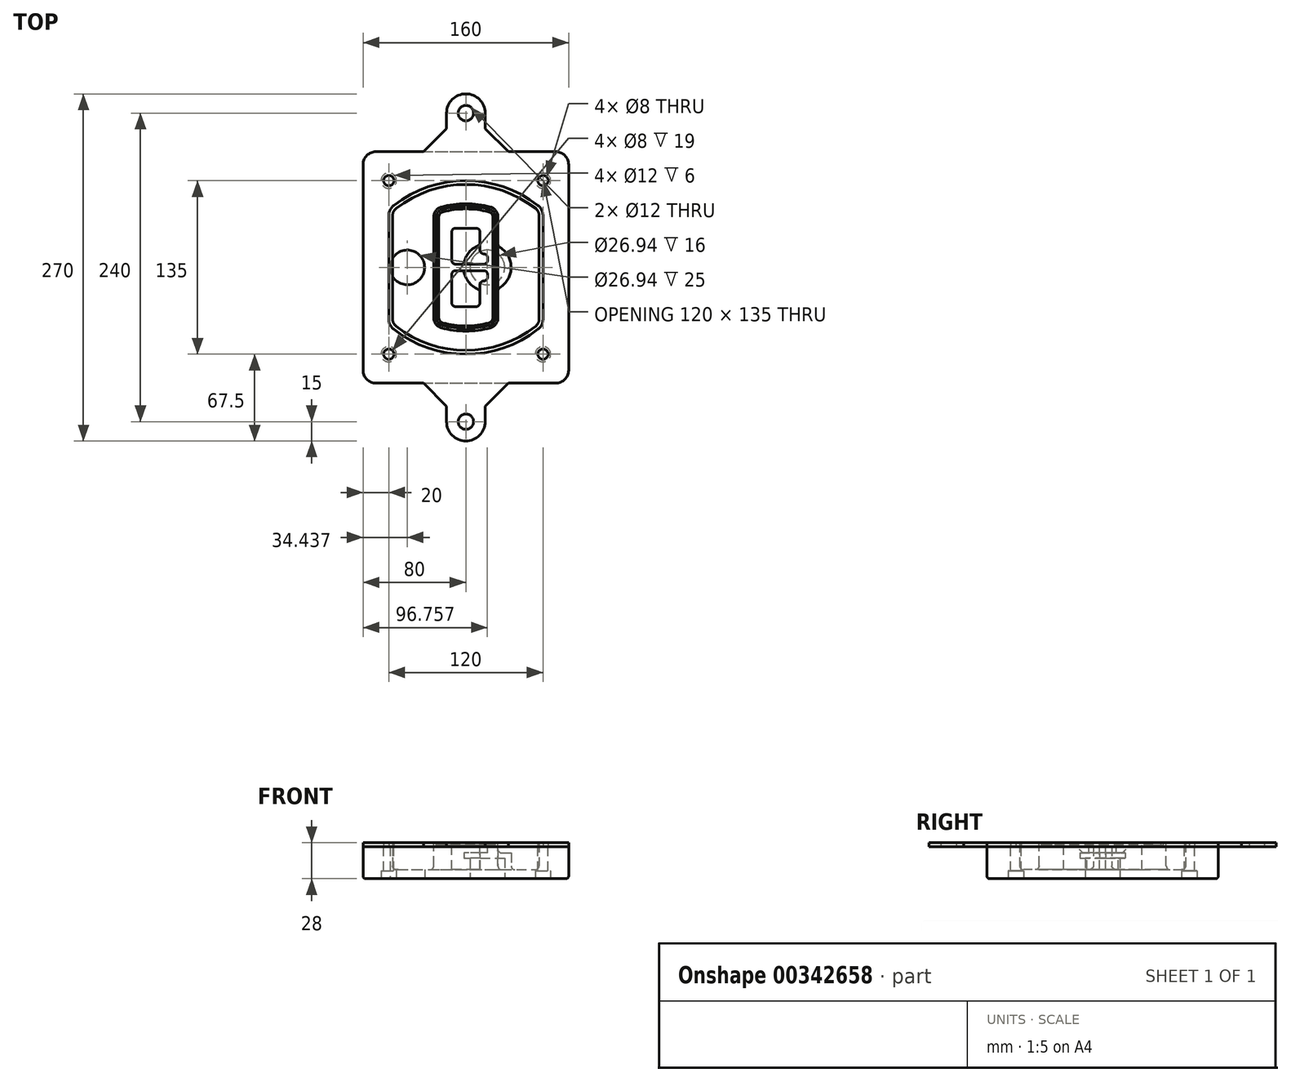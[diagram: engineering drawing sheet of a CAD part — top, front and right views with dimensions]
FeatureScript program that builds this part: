
annotation { "Feature Type Name" : "Feature", "Feature Type Description" : "" }
export const myFeature = defineFeature(function(context is Context, id is Id, definition is map)
    precondition{}
    {
        {
            var Q0;
            Q0=qCreatedBy(makeId("Top.planeOp"),FACE);
            var sketch = newSketch(context, id + "F0", { "sketchPlane" : qUnion([Q0])});
            skPoint(sketch, "E0.rect.middle", {"position": v(0, 0) * mm});
            skLineSegment(sketch, "E1.bottom", {"start": v(-70, -90) * mm, "end": v(70, -90) * mm});
            skLineSegment(sketch, "E1.top", {"start": v(-70, 90) * mm, "end": v(70, 90) * mm});
            skLineSegment(sketch, "E1.left", {"start": v(-80, -80) * mm, "end": v(-80, 80) * mm});
            skLineSegment(sketch, "E1.right", {"start": v(80, -80) * mm, "end": v(80, 80) * mm});
            skLineSegment(sketch, "E2", {"start": v(-80, 90) * mm, "end": v(80, -90) * mm, "construction": true});
            skLineSegment(sketch, "E3", {"start": v(80, 90) * mm, "end": v(-80, -90) * mm, "construction": true});
            skCircle(sketch, "E4", {"center": v(-60, 67.5) * mm, "radius": 4 * mm});
            skCircle(sketch, "E5", {"center": v(60, 67.5) * mm, "radius": 4 * mm});
            skCircle(sketch, "E6", {"center": v(60, -67.5) * mm, "radius": 4 * mm});
            skCircle(sketch, "E7", {"center": v(-60, -67.5) * mm, "radius": 4 * mm});
            skLineSegment(sketch, "E8", {"start": v(-60, 67.5) * mm, "end": v(60, 67.5) * mm, "construction": true});
            skLineSegment(sketch, "E9", {"start": v(60, 67.5) * mm, "end": v(60, -67.5) * mm, "construction": true});
            skLineSegment(sketch, "E10", {"start": v(60, -67.5) * mm, "end": v(-60, -67.5) * mm, "construction": true});
            skLineSegment(sketch, "E11", {"start": v(-60, -67.5) * mm, "end": v(-60, 67.5) * mm, "construction": true});
            skLineSegment(sketch, "E12", {"start": v(-60, 40.3) * mm, "end": v(-60, -40.3) * mm});
            skLineSegment(sketch, "E13", {"start": v(60, 40.3) * mm, "end": v(60, -40.3) * mm});
            skArc(sketch, "E14", {"start": v(56.15, 48.18) * mm, "mid": v(0, 67.5) * mm, "end": v(-56.15, 48.18) * mm});
            skArc(sketch, "E15", {"start": v(-56.15, -48.18) * mm, "mid": v(0, -67.5) * mm, "end": v(56.15, -48.18) * mm});
            skLineSegment(sketch, "E16", {"start": v(-60, 0) * mm, "end": v(60, 0) * mm, "construction": true});
            skPoint(sketch, "E17.visualSharp", {"position": v(-60, -45) * mm});
            skArc(sketch, "E17.filletArc", {"start": v(-60, -40.3) * mm, "mid": v(-58.99, -44.68) * mm, "end": v(-56.15, -48.18) * mm});
            skPoint(sketch, "E18.visualSharp", {"position": v(-60, 45) * mm});
            skArc(sketch, "E18.filletArc", {"start": v(-56.15, 48.18) * mm, "mid": v(-58.99, 44.68) * mm, "end": v(-60, 40.3) * mm});
            skPoint(sketch, "E19.visualSharp", {"position": v(60, 45) * mm});
            skArc(sketch, "E19.filletArc", {"start": v(60, 40.3) * mm, "mid": v(58.99, 44.68) * mm, "end": v(56.15, 48.18) * mm});
            skPoint(sketch, "E20.visualSharp", {"position": v(60, -45) * mm});
            skArc(sketch, "E20.filletArc", {"start": v(56.15, -48.18) * mm, "mid": v(58.99, -44.68) * mm, "end": v(60, -40.3) * mm});
            skPoint(sketch, "E21.visualSharp", {"position": v(-80, 90) * mm});
            skArc(sketch, "E21.filletArc", {"start": v(-70, 90) * mm, "mid": v(-77.07, 87.07) * mm, "end": v(-80, 80) * mm});
            skPoint(sketch, "E22.visualSharp", {"position": v(80, 90) * mm});
            skArc(sketch, "E22.filletArc", {"start": v(80, 80) * mm, "mid": v(77.07, 87.07) * mm, "end": v(70, 90) * mm});
            skPoint(sketch, "E23.visualSharp", {"position": v(80, -90) * mm});
            skArc(sketch, "E23.filletArc", {"start": v(70, -90) * mm, "mid": v(77.07, -87.07) * mm, "end": v(80, -80) * mm});
            skPoint(sketch, "E24.visualSharp", {"position": v(-80, -90) * mm});
            skArc(sketch, "E24.filletArc", {"start": v(-80, -80) * mm, "mid": v(-77.07, -87.07) * mm, "end": v(-70, -90) * mm});
            skArc(sketch, "E25.0", {"start": v(57, 40.3) * mm, "mid": v(56.3, 43.36) * mm, "end": v(54.3, 45.81) * mm});
            skLineSegment(sketch, "E25.1", {"start": v(57, 40.3) * mm, "end": v(57, -40.3) * mm});
            skArc(sketch, "E25.2", {"start": v(54.3, -45.81) * mm, "mid": v(56.3, -43.36) * mm, "end": v(57, -40.3) * mm});
            skArc(sketch, "E25.3", {"start": v(-54.3, -45.81) * mm, "mid": v(0, -64.5) * mm, "end": v(54.3, -45.81) * mm});
            skArc(sketch, "E25.4", {"start": v(-57, -40.3) * mm, "mid": v(-56.3, -43.36) * mm, "end": v(-54.3, -45.81) * mm});
            skArc(sketch, "E25.5", {"start": v(54.3, 45.81) * mm, "mid": v(0, 64.5) * mm, "end": v(-54.3, 45.81) * mm});
            skLineSegment(sketch, "E25.6", {"start": v(-57, 40.3) * mm, "end": v(-57, -40.3) * mm});
            skArc(sketch, "E25.7", {"start": v(-54.3, 45.81) * mm, "mid": v(-56.3, 43.36) * mm, "end": v(-57, 40.3) * mm});
            skArc(sketch, "E26.0", {"start": v(-58.62, 51.33) * mm, "mid": v(-62.58, 46.43) * mm, "end": v(-64, 40.3) * mm});
            skArc(sketch, "E26.1", {"start": v(58.62, 51.33) * mm, "mid": v(0, 71.5) * mm, "end": v(-58.62, 51.33) * mm});
            skArc(sketch, "E26.2", {"start": v(64, 40.3) * mm, "mid": v(62.58, 46.43) * mm, "end": v(58.62, 51.33) * mm});
            skLineSegment(sketch, "E26.3", {"start": v(64, 40.3) * mm, "end": v(64, -40.3) * mm});
            skArc(sketch, "E26.4", {"start": v(58.62, -51.33) * mm, "mid": v(62.58, -46.43) * mm, "end": v(64, -40.3) * mm});
            skLineSegment(sketch, "E26.5", {"start": v(-64, 40.3) * mm, "end": v(-64, -40.3) * mm});
            skArc(sketch, "E26.6", {"start": v(-58.62, -51.33) * mm, "mid": v(0, -71.5) * mm, "end": v(58.62, -51.33) * mm});
            skArc(sketch, "E26.7", {"start": v(-64, -40.3) * mm, "mid": v(-62.58, -46.43) * mm, "end": v(-58.62, -51.33) * mm});
            skSolve(sketch);
        }
        {
            var Q0;
            Q0=makeQuery(id+"F0.imprint","IMPRINT",FACE,{"disambiguationData":[TD([[makeQuery(id+"F0.imprint","IMPRINT",EDGE,{"derivedFrom":sQuery(id+"F0.wireOp",EDGE,"E1.bottom")}),1.0]])]});
            var Q1;
            Q1=makeQuery(id+"F0.imprint","IMPRINT",FACE,{"disambiguationData":[TD([[makeQuery(id+"F0.imprint","IMPRINT",EDGE,{"derivedFrom":sQuery(id+"F0.wireOp",EDGE,"E12")}),1.0]])]});
            var Q2;
            Q2=makeQuery(id+"F0.imprint","IMPRINT",FACE,{"disambiguationData":[TD([[makeQuery(id+"F0.imprint","IMPRINT",EDGE,{"derivedFrom":sQuery(id+"F0.wireOp",EDGE,"E25.0")}),1.0]])]});
            var Q3;
            Q3=makeQuery(id+"F0.imprint","IMPRINT",FACE,{"disambiguationData":[TD([[makeQuery(id+"F0.imprint","IMPRINT",EDGE,{"derivedFrom":sQuery(id+"F0.wireOp",EDGE,"E12")}),-1.0]])]});
            extrude(context, id + "F1", {"entities" : qUnion([Q0, Q1, Q2, Q3]), "oppositeDirection" : true, "depth" : 25 * mm});
        }
        {
            var Q0;
            Q0=makeQuery(id+"F0.imprint","IMPRINT",FACE,{"disambiguationData":[TD([[makeQuery(id+"F0.imprint","IMPRINT",EDGE,{"derivedFrom":sQuery(id+"F0.wireOp",EDGE,"E12")}),1.0]])]});
            extrude(context, id + "F2", {"entities" : qUnion([Q0]), "operationType" : NewBodyOperationType.ADD, "depth" : 3 * mm});
        }
        {
            var Q0;
            Q0=makeQuery(id+"F0.imprint","IMPRINT",FACE,{"disambiguationData":[TD([[makeQuery(id+"F0.imprint","IMPRINT",EDGE,{"derivedFrom":sQuery(id+"F0.wireOp",EDGE,"E25.0")}),1.0]])]});
            extrude(context, id + "F3", {"entities" : qUnion([Q0]), "operationType" : NewBodyOperationType.REMOVE, "oppositeDirection" : true, "depth" : 18 * mm});
        }
        {
            var Q0;
            Q0=makeQuery(id+"F2.opExtrude","CAP_FACE",FACE,{"disambiguationData":[OSD([sQuery(id+"F0.wireOp",EDGE,"E12"),sQuery(id+"F0.wireOp",EDGE,"E13"),sQuery(id+"F0.wireOp",EDGE,"E14"),sQuery(id+"F0.wireOp",EDGE,"E15"),sQuery(id+"F0.wireOp",EDGE,"E17.filletArc"),sQuery(id+"F0.wireOp",EDGE,"E18.filletArc"),sQuery(id+"F0.wireOp",EDGE,"E19.filletArc"),sQuery(id+"F0.wireOp",EDGE,"E20.filletArc"),sQuery(id+"F0.wireOp",EDGE,"E25.0"),sQuery(id+"F0.wireOp",EDGE,"E25.1"),sQuery(id+"F0.wireOp",EDGE,"E25.2"),sQuery(id+"F0.wireOp",EDGE,"E25.3"),sQuery(id+"F0.wireOp",EDGE,"E25.4"),sQuery(id+"F0.wireOp",EDGE,"E25.5"),sQuery(id+"F0.wireOp",EDGE,"E25.6"),sQuery(id+"F0.wireOp",EDGE,"E25.7")])],"isStart":false});
            var sketch = newSketch(context, id + "F4", { "sketchPlane" : qUnion([Q0])});
            skArc(sketch, "E27.0", {"start": v(-19.08, -46.97) * mm, "mid": v(0, -49.5) * mm, "end": v(19.08, -46.97) * mm});
            skArc(sketch, "E28.0", {"start": v(19.08, 46.97) * mm, "mid": v(0, 49.5) * mm, "end": v(-19.08, 46.97) * mm});
            skLineSegment(sketch, "E29", {"start": v(-25, 39.25) * mm, "end": v(-25, -39.25) * mm});
            skLineSegment(sketch, "E30", {"start": v(25, 39.25) * mm, "end": v(25, -39.25) * mm});
            skLineSegment(sketch, "E31", {"start": v(-25, 45.1) * mm, "end": v(25, 45.1) * mm, "construction": true});
            skLineSegment(sketch, "E32", {"start": v(-25, -45.1) * mm, "end": v(25, -45.1) * mm, "construction": true});
            skPoint(sketch, "E33.visualSharp", {"position": v(-25, 45.1) * mm});
            skArc(sketch, "E33.filletArc", {"start": v(-19.08, 46.97) * mm, "mid": v(-23.35, 44.11) * mm, "end": v(-25, 39.25) * mm});
            skPoint(sketch, "E34.visualSharp", {"position": v(25, 45.1) * mm});
            skArc(sketch, "E34.filletArc", {"start": v(25, 39.25) * mm, "mid": v(23.35, 44.11) * mm, "end": v(19.08, 46.97) * mm});
            skPoint(sketch, "E35.visualSharp", {"position": v(25, -45.1) * mm});
            skArc(sketch, "E35.filletArc", {"start": v(19.08, -46.97) * mm, "mid": v(23.35, -44.11) * mm, "end": v(25, -39.25) * mm});
            skPoint(sketch, "E36.visualSharp", {"position": v(-25, -45.1) * mm});
            skArc(sketch, "E36.filletArc", {"start": v(-25, -39.25) * mm, "mid": v(-23.35, -44.11) * mm, "end": v(-19.08, -46.97) * mm});
            skArc(sketch, "E37.0", {"start": v(54.3, 45.81) * mm, "mid": v(0, 64.5) * mm, "end": v(-54.3, 45.81) * mm});
            skArc(sketch, "E37.1", {"start": v(-54.3, 45.81) * mm, "mid": v(-56.3, 43.36) * mm, "end": v(-57, 40.3) * mm});
            skLineSegment(sketch, "E37.2", {"start": v(-57, 40.3) * mm, "end": v(-57, -40.3) * mm});
            skArc(sketch, "E37.3", {"start": v(-57, -40.3) * mm, "mid": v(-56.3, -43.36) * mm, "end": v(-54.3, -45.81) * mm});
            skArc(sketch, "E37.4", {"start": v(-54.3, -45.81) * mm, "mid": v(0, -64.5) * mm, "end": v(54.3, -45.81) * mm});
            skArc(sketch, "E37.5", {"start": v(54.3, -45.81) * mm, "mid": v(56.3, -43.36) * mm, "end": v(57, -40.3) * mm});
            skLineSegment(sketch, "E37.6", {"start": v(57, 40.3) * mm, "end": v(57, -40.3) * mm});
            skArc(sketch, "E37.7", {"start": v(57, 40.3) * mm, "mid": v(56.3, 43.36) * mm, "end": v(54.3, 45.81) * mm});
            skLineSegment(sketch, "E38.0", {"start": v(23, 39.25) * mm, "end": v(23, -39.25) * mm});
            skArc(sketch, "E38.1", {"start": v(18.56, -45.04) * mm, "mid": v(21.76, -42.9) * mm, "end": v(23, -39.25) * mm});
            skArc(sketch, "E38.2", {"start": v(-18.56, -45.04) * mm, "mid": v(0, -47.5) * mm, "end": v(18.56, -45.04) * mm});
            skArc(sketch, "E38.3", {"start": v(-23, -39.25) * mm, "mid": v(-21.76, -42.9) * mm, "end": v(-18.56, -45.04) * mm});
            skLineSegment(sketch, "E38.4", {"start": v(-23, 39.25) * mm, "end": v(-23, -39.25) * mm});
            skArc(sketch, "E38.5", {"start": v(23, 39.25) * mm, "mid": v(21.76, 42.9) * mm, "end": v(18.56, 45.04) * mm});
            skArc(sketch, "E38.6", {"start": v(-18.56, 45.04) * mm, "mid": v(-21.76, 42.9) * mm, "end": v(-23, 39.25) * mm});
            skArc(sketch, "E38.7", {"start": v(18.56, 45.04) * mm, "mid": v(0, 47.5) * mm, "end": v(-18.56, 45.04) * mm});
            skArc(sketch, "E39.0", {"start": v(21, 39.25) * mm, "mid": v(20.18, 41.68) * mm, "end": v(18.04, 43.1) * mm});
            skLineSegment(sketch, "E39.1", {"start": v(21, 39.25) * mm, "end": v(21, -39.25) * mm});
            skArc(sketch, "E39.2", {"start": v(18.04, -43.1) * mm, "mid": v(20.18, -41.68) * mm, "end": v(21, -39.25) * mm});
            skArc(sketch, "E39.3", {"start": v(-18.04, -43.1) * mm, "mid": v(0, -45.5) * mm, "end": v(18.04, -43.1) * mm});
            skArc(sketch, "E39.4", {"start": v(-21, -39.25) * mm, "mid": v(-20.18, -41.68) * mm, "end": v(-18.04, -43.1) * mm});
            skArc(sketch, "E39.5", {"start": v(18.04, 43.1) * mm, "mid": v(0, 45.5) * mm, "end": v(-18.04, 43.1) * mm});
            skLineSegment(sketch, "E39.6", {"start": v(-21, 39.25) * mm, "end": v(-21, -39.25) * mm});
            skArc(sketch, "E39.7", {"start": v(-18.04, 43.1) * mm, "mid": v(-20.18, 41.68) * mm, "end": v(-21, 39.25) * mm});
            skLineSegment(sketch, "E40", {"start": v(-25, 0) * mm, "end": v(25, 0) * mm, "construction": true});
            skLineSegment(sketch, "E41", {"start": v(-11, 5.5) * mm, "end": v(-11, 27.5) * mm});
            skLineSegment(sketch, "E42", {"start": v(-8, 30.5) * mm, "end": v(8, 30.5) * mm});
            skLineSegment(sketch, "E43", {"start": v(11, 27.5) * mm, "end": v(11, 13.5) * mm});
            skLineSegment(sketch, "E44", {"start": v(14, 10.5) * mm, "end": v(14, 10.5) * mm});
            skLineSegment(sketch, "E45", {"start": v(17, 7.5) * mm, "end": v(17, 5.5) * mm});
            skLineSegment(sketch, "E46", {"start": v(14, 2.5) * mm, "end": v(-8, 2.5) * mm});
            skPoint(sketch, "E47.visualSharp", {"position": v(-11, 30.5) * mm});
            skArc(sketch, "E47.filletArc", {"start": v(-8, 30.5) * mm, "mid": v(-10.12, 29.62) * mm, "end": v(-11, 27.5) * mm});
            skPoint(sketch, "E48.visualSharp", {"position": v(11, 30.5) * mm});
            skArc(sketch, "E48.filletArc", {"start": v(11, 27.5) * mm, "mid": v(10.12, 29.62) * mm, "end": v(8, 30.5) * mm});
            skPoint(sketch, "E49.visualSharp", {"position": v(11, 10.5) * mm});
            skArc(sketch, "E49.filletArc", {"start": v(11, 13.5) * mm, "mid": v(11.88, 11.38) * mm, "end": v(14, 10.5) * mm});
            skPoint(sketch, "E50.visualSharp", {"position": v(17, 10.5) * mm});
            skArc(sketch, "E50.filletArc", {"start": v(17, 7.5) * mm, "mid": v(16.12, 9.62) * mm, "end": v(14, 10.5) * mm});
            skPoint(sketch, "E51.visualSharp", {"position": v(17, 2.5) * mm});
            skArc(sketch, "E51.filletArc", {"start": v(14, 2.5) * mm, "mid": v(16.12, 3.38) * mm, "end": v(17, 5.5) * mm});
            skPoint(sketch, "E52.visualSharp", {"position": v(-11, 2.5) * mm});
            skArc(sketch, "E52.filletArc", {"start": v(-11, 5.5) * mm, "mid": v(-10.12, 3.38) * mm, "end": v(-8, 2.5) * mm});
            skLineSegment(sketch, "E53.0.MirrorCS", {"start": v(14, -2.5) * mm, "end": v(-8, -2.5) * mm});
            skArc(sketch, "E54.0.MirrorCS", {"start": v(-11, -5.5) * mm, "mid": v(-10.12, -3.38) * mm, "end": v(-8, -2.5) * mm});
            skLineSegment(sketch, "E55.0.MirrorCS", {"start": v(-11, -5.5) * mm, "end": v(-11, -27.5) * mm});
            skArc(sketch, "E56.0.MirrorCS", {"start": v(-8, -30.5) * mm, "mid": v(-10.12, -29.62) * mm, "end": v(-11, -27.5) * mm});
            skLineSegment(sketch, "E57.0.MirrorCS", {"start": v(-8, -30.5) * mm, "end": v(8, -30.5) * mm});
            skArc(sketch, "E58.0.MirrorCS", {"start": v(11, -27.5) * mm, "mid": v(10.12, -29.62) * mm, "end": v(8, -30.5) * mm});
            skLineSegment(sketch, "E59.0.MirrorCS", {"start": v(11, -27.5) * mm, "end": v(11, -13.5) * mm});
            skArc(sketch, "E60.0.MirrorCS", {"start": v(11, -13.5) * mm, "mid": v(11.88, -11.38) * mm, "end": v(14, -10.5) * mm});
            skArc(sketch, "E61.0.MirrorCS", {"start": v(17, -7.5) * mm, "mid": v(16.12, -9.62) * mm, "end": v(14, -10.5) * mm});
            skLineSegment(sketch, "E62.0.MirrorCS", {"start": v(17, -7.5) * mm, "end": v(17, -5.5) * mm});
            skArc(sketch, "E63.0.MirrorCS", {"start": v(14, -2.5) * mm, "mid": v(16.12, -3.38) * mm, "end": v(17, -5.5) * mm});
            skSolve(sketch);
        }
        {
            var Q0;
            Q0=makeQuery(id+"F4.imprint","IMPRINT",FACE,{"disambiguationData":[TD([[makeQuery(id+"F4.imprint","IMPRINT",EDGE,{"derivedFrom":sQuery(id+"F4.wireOp",EDGE,"E27.0")}),1.0]])]});
            var Q1;
            Q1=makeQuery(id+"F4.imprint","IMPRINT",FACE,{"disambiguationData":[TD([[makeQuery(id+"F4.imprint","IMPRINT",EDGE,{"derivedFrom":sQuery(id+"F4.wireOp",EDGE,"E38.0")}),-1.0]])]});
            var Q2;
            Q2=makeQuery(id+"F4.imprint","IMPRINT",FACE,{"disambiguationData":[TD([[makeQuery(id+"F4.imprint","IMPRINT",EDGE,{"derivedFrom":sQuery(id+"F4.wireOp",EDGE,"E39.0")}),1.0]])]});
            extrude(context, id + "F5", {"entities" : qUnion([Q0, Q1, Q2]), "operationType" : NewBodyOperationType.ADD, "endBound" : BoundingType.UP_TO_NEXT, "oppositeDirection" : true, "depth" : 25 * mm});
        }
        {
            var Q0;
            Q0=makeQuery(id+"F4.imprint","IMPRINT",FACE,{"disambiguationData":[TD([[makeQuery(id+"F4.imprint","IMPRINT",EDGE,{"derivedFrom":sQuery(id+"F4.wireOp",EDGE,"E38.0")}),-1.0]])]});
            extrude(context, id + "F6", {"entities" : qUnion([Q0]), "operationType" : NewBodyOperationType.REMOVE, "oppositeDirection" : true, "depth" : 2 * mm});
        }
        {
            var Q0;
            Q0=makeQuery(id+"F1.opExtrude","CAP_FACE",FACE,{"disambiguationData":[OSD([sQuery(id+"F0.wireOp",EDGE,"E1.bottom"),sQuery(id+"F0.wireOp",EDGE,"E1.top"),sQuery(id+"F0.wireOp",EDGE,"E1.left"),sQuery(id+"F0.wireOp",EDGE,"E1.right"),sQuery(id+"F0.wireOp",EDGE,"E4"),sQuery(id+"F0.wireOp",EDGE,"E5"),sQuery(id+"F0.wireOp",EDGE,"E6"),sQuery(id+"F0.wireOp",EDGE,"E7"),sQuery(id+"F0.wireOp",EDGE,"E21.filletArc"),sQuery(id+"F0.wireOp",EDGE,"E22.filletArc"),sQuery(id+"F0.wireOp",EDGE,"E23.filletArc"),sQuery(id+"F0.wireOp",EDGE,"E24.filletArc")])],"isStart":false});
            var sketch = newSketch(context, id + "F7", { "sketchPlane" : qUnion([Q0])});
            skCircle(sketch, "E64", {"center": v(16.76, 0) * mm, "radius": 13.47 * mm});
            skCircle(sketch, "E65", {"center": v(-45.56, 0) * mm, "radius": 13.47 * mm});
            skLineSegment(sketch, "E66", {"start": v(80, 0) * mm, "end": v(-80, 0) * mm});
            skCircle(sketch, "E67", {"center": v(16.76, 0) * mm, "radius": 18.47 * mm});
            skCircle(sketch, "E68", {"center": v(60, -67.5) * mm, "radius": 6 * mm});
            skCircle(sketch, "E69", {"center": v(-60, -67.5) * mm, "radius": 6 * mm});
            skCircle(sketch, "E70", {"center": v(-60, 67.5) * mm, "radius": 6 * mm});
            skCircle(sketch, "E71", {"center": v(60, 67.5) * mm, "radius": 6 * mm});
            skSolve(sketch);
        }
        {
            var Q0;
            {var subQ1=sQuery(id+"F7.wireOp",EDGE,"E66");var subQ4=sQuery(id+"F7.wireOp",EDGE,"E64");var subQ6=makeQuery(id+"F7.imprint","INTERSECT",VERTEX,{"disambiguationData":[OD(0.0)],"derivedFrom":[subQ4,subQ1]});Q0=makeQuery(id+"F7.imprint","IMPRINT",FACE,{"disambiguationData":[TD([[makeQuery(id+"F7.imprint","IMPRINT",EDGE,{"disambiguationData":[TD([[subQ6,-1.0]])],"derivedFrom":subQ4}),-1.0]])]});}
            var Q1;
            {var subQ0=sQuery(id+"F7.wireOp",EDGE,"E66");var subQ1=sQuery(id+"F7.wireOp",EDGE,"E64");var subQ3=makeQuery(id+"F7.imprint","INTERSECT",VERTEX,{"disambiguationData":[OD(0.0)],"derivedFrom":[subQ1,subQ0]});Q1=makeQuery(id+"F7.imprint","IMPRINT",FACE,{"disambiguationData":[TD([[makeQuery(id+"F7.imprint","IMPRINT",EDGE,{"disambiguationData":[TD([[subQ3,-1.0]])],"derivedFrom":subQ1}),1.0]])]});}
            var Q2;
            {var subQ0=sQuery(id+"F7.wireOp",EDGE,"E66");var subQ1=sQuery(id+"F7.wireOp",EDGE,"E64");var subQ3=makeQuery(id+"F7.imprint","INTERSECT",VERTEX,{"disambiguationData":[OD(0.0)],"derivedFrom":[subQ1,subQ0]});Q2=makeQuery(id+"F7.imprint","IMPRINT",FACE,{"disambiguationData":[TD([[makeQuery(id+"F7.imprint","IMPRINT",EDGE,{"disambiguationData":[TD([[subQ3,1.0]])],"derivedFrom":subQ1}),1.0]])]});}
            var Q3;
            {var subQ1=sQuery(id+"F7.wireOp",EDGE,"E66");var subQ4=sQuery(id+"F7.wireOp",EDGE,"E64");var subQ6=makeQuery(id+"F7.imprint","INTERSECT",VERTEX,{"disambiguationData":[OD(0.0)],"derivedFrom":[subQ4,subQ1]});Q3=makeQuery(id+"F7.imprint","IMPRINT",FACE,{"disambiguationData":[TD([[makeQuery(id+"F7.imprint","IMPRINT",EDGE,{"disambiguationData":[TD([[subQ6,1.0]])],"derivedFrom":subQ4}),-1.0]])]});}
            extrude(context, id + "F8", {"entities" : qUnion([Q0, Q1, Q2, Q3]), "operationType" : NewBodyOperationType.ADD, "oppositeDirection" : true, "depth" : 20 * mm});
        }
        {
            var Q0;
            {var subQ0=sQuery(id+"F7.wireOp",EDGE,"E66");var subQ1=sQuery(id+"F7.wireOp",EDGE,"E64");var subQ3=makeQuery(id+"F7.imprint","INTERSECT",VERTEX,{"disambiguationData":[OD(0.0)],"derivedFrom":[subQ1,subQ0]});Q0=makeQuery(id+"F7.imprint","IMPRINT",FACE,{"disambiguationData":[TD([[makeQuery(id+"F7.imprint","IMPRINT",EDGE,{"disambiguationData":[TD([[subQ3,-1.0]])],"derivedFrom":subQ1}),1.0]])]});}
            var Q1;
            {var subQ0=sQuery(id+"F7.wireOp",EDGE,"E66");var subQ1=sQuery(id+"F7.wireOp",EDGE,"E64");var subQ3=makeQuery(id+"F7.imprint","INTERSECT",VERTEX,{"disambiguationData":[OD(0.0)],"derivedFrom":[subQ1,subQ0]});Q1=makeQuery(id+"F7.imprint","IMPRINT",FACE,{"disambiguationData":[TD([[makeQuery(id+"F7.imprint","IMPRINT",EDGE,{"disambiguationData":[TD([[subQ3,1.0]])],"derivedFrom":subQ1}),1.0]])]});}
            extrude(context, id + "F9", {"entities" : qUnion([Q0, Q1]), "operationType" : NewBodyOperationType.REMOVE, "oppositeDirection" : true, "depth" : 16 * mm});
        }
        {
            var Q0;
            {var subQ0=sQuery(id+"F7.wireOp",EDGE,"E66");var subQ1=sQuery(id+"F7.wireOp",EDGE,"E65");var subQ3=makeQuery(id+"F7.imprint","INTERSECT",VERTEX,{"disambiguationData":[OD(0.0)],"derivedFrom":[subQ1,subQ0]});Q0=makeQuery(id+"F7.imprint","IMPRINT",FACE,{"disambiguationData":[TD([[makeQuery(id+"F7.imprint","IMPRINT",EDGE,{"disambiguationData":[TD([[subQ3,-1.0]])],"derivedFrom":subQ1}),1.0]])]});}
            var Q1;
            {var subQ0=sQuery(id+"F7.wireOp",EDGE,"E66");var subQ1=sQuery(id+"F7.wireOp",EDGE,"E65");var subQ3=makeQuery(id+"F7.imprint","INTERSECT",VERTEX,{"disambiguationData":[OD(0.0)],"derivedFrom":[subQ1,subQ0]});Q1=makeQuery(id+"F7.imprint","IMPRINT",FACE,{"disambiguationData":[TD([[makeQuery(id+"F7.imprint","IMPRINT",EDGE,{"disambiguationData":[TD([[subQ3,1.0]])],"derivedFrom":subQ1}),1.0]])]});}
            extrude(context, id + "F10", {"entities" : qUnion([Q0, Q1]), "operationType" : NewBodyOperationType.REMOVE, "oppositeDirection" : true, "depth" : 25 * mm});
        }
        {
            var Q0;
            Q0=makeQuery(id+"F7.imprint","IMPRINT",FACE,{"disambiguationData":[TD([[makeQuery(id+"F7.imprint","IMPRINT",EDGE,{"derivedFrom":sQuery(id+"F7.wireOp",EDGE,"E68")}),1.0]])]});
            var Q1;
            Q1=makeQuery(id+"F7.imprint","IMPRINT",FACE,{"disambiguationData":[TD([[makeQuery(id+"F7.imprint","IMPRINT",EDGE,{"derivedFrom":makeQuery(id+"F1.opExtrude","CAP_EDGE",EDGE,{"disambiguationData":[OSD([sQuery(id+"F0.wireOp",EDGE,"E5")])],"isStart":false})}),-1.0]])]});
            var Q2;
            Q2=makeQuery(id+"F7.imprint","IMPRINT",FACE,{"disambiguationData":[TD([[makeQuery(id+"F7.imprint","IMPRINT",EDGE,{"derivedFrom":sQuery(id+"F7.wireOp",EDGE,"E69")}),1.0]])]});
            var Q3;
            Q3=makeQuery(id+"F7.imprint","IMPRINT",FACE,{"disambiguationData":[TD([[makeQuery(id+"F7.imprint","IMPRINT",EDGE,{"derivedFrom":makeQuery(id+"F1.opExtrude","CAP_EDGE",EDGE,{"disambiguationData":[OSD([sQuery(id+"F0.wireOp",EDGE,"E4")])],"isStart":false})}),-1.0]])]});
            var Q4;
            Q4=makeQuery(id+"F7.imprint","IMPRINT",FACE,{"disambiguationData":[TD([[makeQuery(id+"F7.imprint","IMPRINT",EDGE,{"derivedFrom":sQuery(id+"F7.wireOp",EDGE,"E70")}),1.0]])]});
            var Q5;
            Q5=makeQuery(id+"F7.imprint","IMPRINT",FACE,{"disambiguationData":[TD([[makeQuery(id+"F7.imprint","IMPRINT",EDGE,{"derivedFrom":makeQuery(id+"F1.opExtrude","CAP_EDGE",EDGE,{"disambiguationData":[OSD([sQuery(id+"F0.wireOp",EDGE,"E7")])],"isStart":false})}),-1.0]])]});
            var Q6;
            Q6=makeQuery(id+"F7.imprint","IMPRINT",FACE,{"disambiguationData":[TD([[makeQuery(id+"F7.imprint","IMPRINT",EDGE,{"derivedFrom":sQuery(id+"F7.wireOp",EDGE,"E71")}),1.0]])]});
            var Q7;
            Q7=makeQuery(id+"F7.imprint","IMPRINT",FACE,{"disambiguationData":[TD([[makeQuery(id+"F7.imprint","IMPRINT",EDGE,{"derivedFrom":makeQuery(id+"F1.opExtrude","CAP_EDGE",EDGE,{"disambiguationData":[OSD([sQuery(id+"F0.wireOp",EDGE,"E6")])],"isStart":false})}),-1.0]])]});
            extrude(context, id + "F11", {"entities" : qUnion([Q0, Q1, Q2, Q3, Q4, Q5, Q6, Q7]), "operationType" : NewBodyOperationType.REMOVE, "oppositeDirection" : true, "depth" : 6 * mm});
        }
        {
            var Q0;
            Q0=makeQuery(id+"F9.boolean.opBoolean","COPY",FACE,{"derivedFrom":makeQuery(id+"F9.opExtrude","CAP_FACE",FACE,{"disambiguationData":[OSD([sQuery(id+"F7.wireOp",EDGE,"E64")])],"isStart":false})});
            var sketch = newSketch(context, id + "F12", { "sketchPlane" : qUnion([Q0])});
            skArc(sketch, "E72.0", {"start": v(11, 17.55) * mm, "mid": v(2.57, 11.82) * mm, "end": v(-1.54, 2.5) * mm});
            skArc(sketch, "E72.1", {"start": v(-1.54, -2.5) * mm, "mid": v(2.57, -11.82) * mm, "end": v(11, -17.55) * mm});
            skLineSegment(sketch, "E73", {"start": v(-1.54, -2.5) * mm, "end": v(14, -2.5) * mm});
            skLineSegment(sketch, "E74.0", {"start": v(14, 2.5) * mm, "end": v(-1.54, 2.5) * mm});
            skArc(sketch, "E74.1", {"start": v(14, 2.5) * mm, "mid": v(16.12, 3.38) * mm, "end": v(17, 5.5) * mm});
            skLineSegment(sketch, "E74.2", {"start": v(17, 7.5) * mm, "end": v(17, 5.5) * mm});
            skArc(sketch, "E74.3", {"start": v(17, 7.5) * mm, "mid": v(16.12, 9.62) * mm, "end": v(14, 10.5) * mm});
            skArc(sketch, "E74.4", {"start": v(11, 13.5) * mm, "mid": v(11.88, 11.38) * mm, "end": v(14, 10.5) * mm});
            skLineSegment(sketch, "E74.5", {"start": v(11, 17.55) * mm, "end": v(11, 13.5) * mm});
            skLineSegment(sketch, "E74.7", {"start": v(14, -2.5) * mm, "end": v(-1.54, -2.5) * mm});
            skArc(sketch, "E74.8", {"start": v(14, -2.5) * mm, "mid": v(16.12, -3.38) * mm, "end": v(17, -5.5) * mm});
            skLineSegment(sketch, "E74.9", {"start": v(17, -7.5) * mm, "end": v(17, -5.5) * mm});
            skArc(sketch, "E74.10", {"start": v(17, -7.5) * mm, "mid": v(16.12, -9.62) * mm, "end": v(14, -10.5) * mm});
            skArc(sketch, "E74.11", {"start": v(11, -13.5) * mm, "mid": v(11.88, -11.38) * mm, "end": v(14, -10.5) * mm});
            skLineSegment(sketch, "E74.12", {"start": v(11, -17.55) * mm, "end": v(11, -13.5) * mm});
            skPoint(sketch, "E75.orphan", {"position": v(11, -27.5) * mm});
            skPoint(sketch, "E76.orphan", {"position": v(-8, -2.5) * mm});
            skPoint(sketch, "E77.orphan", {"position": v(-8, 2.5) * mm});
            skPoint(sketch, "E78.orphan", {"position": v(11, 27.5) * mm});
            skSolve(sketch);
        }
        {
            var Q0;
            {var subQ7=sQuery(id+"F12.wireOp",EDGE,"E72.0");var subQ14=sQuery(id+"F12.wireOp",EDGE,"E72.1");var subQ16=sQuery(id+"F12.wireOp",EDGE,"E74.1");var subQ18=sQuery(id+"F12.wireOp",EDGE,"E74.8");Q0=qUnion([makeQuery(id+"F12.imprint","IMPRINT",FACE,{"disambiguationData":[TD([[makeQuery(id+"F12.imprint","IMPRINT",EDGE,{"derivedFrom":subQ7}),1.0]])]}),makeQuery(id+"F12.imprint","IMPRINT",FACE,{"disambiguationData":[TD([[makeQuery(id+"F12.imprint","IMPRINT",EDGE,{"derivedFrom":subQ14}),1.0]])]}),makeQuery(id+"F12.imprint","IMPRINT",FACE,{"disambiguationData":[TD([[makeQuery(id+"F12.imprint","IMPRINT",EDGE,{"derivedFrom":subQ16}),1.0]])]}),makeQuery(id+"F12.imprint","IMPRINT",FACE,{"disambiguationData":[TD([[makeQuery(id+"F12.imprint","IMPRINT",EDGE,{"derivedFrom":subQ18}),-1.0]])]})]);}
            var Q1;
            Q1=makeQuery(id+"F5.boolean.opBoolean","SPLIT",FACE,{"disambiguationData":[TD([makeQuery(id+"F5.opExtrude","SWEPT_FACE",FACE,{"disambiguationData":[OSD([sQuery(id+"F4.wireOp",EDGE,"E41")])]})])],"derivedFrom":makeQuery(id+"F3.boolean.opBoolean","COPY",FACE,{"derivedFrom":makeQuery(id+"F3.opExtrude","CAP_FACE",FACE,{"disambiguationData":[OSD([sQuery(id+"F0.wireOp",EDGE,"E25.0"),sQuery(id+"F0.wireOp",EDGE,"E25.1"),sQuery(id+"F0.wireOp",EDGE,"E25.2"),sQuery(id+"F0.wireOp",EDGE,"E25.3"),sQuery(id+"F0.wireOp",EDGE,"E25.4"),sQuery(id+"F0.wireOp",EDGE,"E25.5"),sQuery(id+"F0.wireOp",EDGE,"E25.6"),sQuery(id+"F0.wireOp",EDGE,"E25.7")])],"isStart":false})})});
            extrude(context, id + "F13", {"entities" : qUnion([Q0]), "operationType" : NewBodyOperationType.REMOVE, "endBound" : BoundingType.UP_TO_SURFACE, "endBoundEntityFace" : qUnion([Q1]), "depth" : 25 * mm});
        }
        {
            var Q0;
            Q0=makeQuery(id+"F3.boolean.opBoolean","COPY",EDGE,{"derivedFrom":makeQuery(id+"F3.opExtrude","CAP_EDGE",EDGE,{"disambiguationData":[OSD([sQuery(id+"F0.wireOp",EDGE,"E25.6")])],"isStart":false})});
            var Q1;
            Q1=makeQuery(id+"F8.boolean.opBoolean","INTERSECT",EDGE,{"derivedFrom":[makeQuery(id+"F5.opExtrude","SWEPT_FACE",FACE,{"disambiguationData":[OSD([sQuery(id+"F4.wireOp",EDGE,"E30")])]}),makeQuery(id+"F8.opExtrude","CAP_FACE",FACE,{"disambiguationData":[OSD([sQuery(id+"F7.wireOp",EDGE,"E67")])],"isStart":false})]});
            var Q2;
            Q2=makeQuery(id+"F8.boolean.opBoolean","INTERSECT",EDGE,{"disambiguationData":[OD(1.0)],"derivedFrom":[makeQuery(id+"F5.opExtrude","SWEPT_FACE",FACE,{"disambiguationData":[OSD([sQuery(id+"F4.wireOp",EDGE,"E30")])]}),makeQuery(id+"F8.opExtrude","SWEPT_FACE",FACE,{"disambiguationData":[OSD([sQuery(id+"F7.wireOp",EDGE,"E67")])]})]});
            var Q3;
            {var subQ0=sQuery(id+"F4.wireOp",EDGE,"E30");Q3=makeQuery(id+"F8.boolean.opBoolean","SPLIT",EDGE,{"disambiguationData":[TD([makeQuery(id+"F5.opExtrude","SWEPT_FACE",FACE,{"disambiguationData":[OSD([sQuery(id+"F4.wireOp",EDGE,"E35.filletArc")])]})])],"derivedFrom":makeQuery(id+"F5.opExtrude","CAP_EDGE",EDGE,{"disambiguationData":[OSD([subQ0])],"isStart":false})});}
            var Q4;
            {var subQ0=sQuery(id+"F0.wireOp",EDGE,"E25.7");var subQ1=sQuery(id+"F0.wireOp",EDGE,"E25.1");var subQ2=sQuery(id+"F0.wireOp",EDGE,"E25.6");var subQ3=sQuery(id+"F0.wireOp",EDGE,"E25.5");var subQ4=sQuery(id+"F0.wireOp",EDGE,"E25.4");var subQ5=sQuery(id+"F0.wireOp",EDGE,"E25.0");var subQ6=sQuery(id+"F0.wireOp",EDGE,"E25.2");var subQ7=sQuery(id+"F0.wireOp",EDGE,"E25.3");Q4=makeQuery(id+"F8.boolean.opBoolean","INTERSECT",EDGE,{"derivedFrom":[makeQuery(id+"F5.boolean.opBoolean","SPLIT",FACE,{"disambiguationData":[TD([makeQuery(id+"F2.opExtrude","SWEPT_FACE",FACE,{"disambiguationData":[OSD([subQ5])]})])],"derivedFrom":makeQuery(id+"F3.boolean.opBoolean","COPY",FACE,{"derivedFrom":makeQuery(id+"F3.opExtrude","CAP_FACE",FACE,{"disambiguationData":[OSD([subQ5,subQ1,subQ6,subQ7,subQ4,subQ3,subQ2,subQ0])],"isStart":false})})}),makeQuery(id+"F8.opExtrude","SWEPT_FACE",FACE,{"disambiguationData":[OSD([sQuery(id+"F7.wireOp",EDGE,"E67")])]})]});}
            var Q5;
            Q5=makeQuery(id+"F8.boolean.opBoolean","INTERSECT",EDGE,{"disambiguationData":[OD(0.0)],"derivedFrom":[makeQuery(id+"F5.opExtrude","SWEPT_FACE",FACE,{"disambiguationData":[OSD([sQuery(id+"F4.wireOp",EDGE,"E30")])]}),makeQuery(id+"F8.opExtrude","SWEPT_FACE",FACE,{"disambiguationData":[OSD([sQuery(id+"F7.wireOp",EDGE,"E67")])]})]});
            fillet(context, id + "F14", {"entities" : qUnion([Q0, Q1, Q2, Q3, Q4, Q5]), "radius" : 3 * mm, "tangentPropagation" : true, "allowEdgeOverflow" : false});
        }
        {
            var Q0;
            Q0=makeQuery(id+"F1.opExtrude","CAP_EDGE",EDGE,{"disambiguationData":[OSD([sQuery(id+"F0.wireOp",EDGE,"E1.bottom")])],"isStart":false});
            fillet(context, id + "F15", {"entities" : qUnion([Q0]), "radius" : 2 * mm, "tangentPropagation" : true, "allowEdgeOverflow" : false});
        }
        {
            var Q0;
            {var subQ0=sQuery(id+"F0.wireOp",EDGE,"E21.filletArc");var subQ1=sQuery(id+"F0.wireOp",EDGE,"E7");var subQ2=sQuery(id+"F0.wireOp",EDGE,"E6");var subQ3=sQuery(id+"F0.wireOp",EDGE,"E5");var subQ4=sQuery(id+"F0.wireOp",EDGE,"E4");var subQ5=sQuery(id+"F0.wireOp",EDGE,"E22.filletArc");var subQ6=sQuery(id+"F0.wireOp",EDGE,"E1.bottom");var subQ7=sQuery(id+"F0.wireOp",EDGE,"E1.right");var subQ8=sQuery(id+"F0.wireOp",EDGE,"E1.top");var subQ9=sQuery(id+"F0.wireOp",EDGE,"E1.left");var subQ10=sQuery(id+"F0.wireOp",EDGE,"E23.filletArc");var subQ11=sQuery(id+"F0.wireOp",EDGE,"E24.filletArc");Q0=makeQuery(id+"F2.boolean.opBoolean","SPLIT",FACE,{"disambiguationData":[TD([makeQuery(id+"F1.opExtrude","SWEPT_FACE",FACE,{"disambiguationData":[OSD([subQ6])]})])],"derivedFrom":makeQuery(id+"F1.opExtrude","CAP_FACE",FACE,{"disambiguationData":[OSD([subQ6,subQ8,subQ9,subQ7,subQ4,subQ3,subQ2,subQ1,subQ0,subQ5,subQ10,subQ11])],"isStart":true})});}
            var sketch = newSketch(context, id + "F16", { "sketchPlane" : qUnion([Q0])});
            skLineSegment(sketch, "E79.0", {"start": v(-70, -90) * mm, "end": v(70, -90) * mm});
            skArc(sketch, "E79.1", {"start": v(-56.15, -48.18) * mm, "mid": v(0, -67.5) * mm, "end": v(56.15, -48.18) * mm});
            skArc(sketch, "E79.2", {"start": v(56.15, -48.18) * mm, "mid": v(58.99, -44.68) * mm, "end": v(60, -40.3) * mm});
            skLineSegment(sketch, "E79.3", {"start": v(60, 40.3) * mm, "end": v(60, -40.3) * mm});
            skLineSegment(sketch, "E79.4", {"start": v(80, -80) * mm, "end": v(80, 80) * mm});
            skArc(sketch, "E79.5", {"start": v(70, -90) * mm, "mid": v(77.07, -87.07) * mm, "end": v(80, -80) * mm});
            skCircle(sketch, "E79.6", {"center": v(60, -67.5) * mm, "radius": 4 * mm});
            skCircle(sketch, "E79.7", {"center": v(-60, -67.5) * mm, "radius": 4 * mm});
            skArc(sketch, "E79.8", {"start": v(-80, -80) * mm, "mid": v(-77.07, -87.07) * mm, "end": v(-70, -90) * mm});
            skLineSegment(sketch, "E79.9", {"start": v(-80, -80) * mm, "end": v(-80, 80) * mm});
            skArc(sketch, "E79.10", {"start": v(-60, -40.3) * mm, "mid": v(-58.99, -44.68) * mm, "end": v(-56.15, -48.18) * mm});
            skLineSegment(sketch, "E79.11", {"start": v(-60, 40.3) * mm, "end": v(-60, -40.3) * mm});
            skArc(sketch, "E79.12", {"start": v(-56.15, 48.18) * mm, "mid": v(-58.99, 44.68) * mm, "end": v(-60, 40.3) * mm});
            skArc(sketch, "E79.13", {"start": v(56.15, 48.18) * mm, "mid": v(0, 67.5) * mm, "end": v(-56.15, 48.18) * mm});
            skArc(sketch, "E79.14", {"start": v(60, 40.3) * mm, "mid": v(58.99, 44.68) * mm, "end": v(56.15, 48.18) * mm});
            skCircle(sketch, "E79.15", {"center": v(60, 67.5) * mm, "radius": 4 * mm});
            skArc(sketch, "E79.16", {"start": v(80, 80) * mm, "mid": v(77.07, 87.07) * mm, "end": v(70, 90) * mm});
            skLineSegment(sketch, "E79.17", {"start": v(-70, 90) * mm, "end": v(70, 90) * mm});
            skArc(sketch, "E79.18", {"start": v(-70, 90) * mm, "mid": v(-77.07, 87.07) * mm, "end": v(-80, 80) * mm});
            skCircle(sketch, "E79.19", {"center": v(-60, 67.5) * mm, "radius": 4 * mm});
            skLineSegment(sketch, "E80", {"start": v(0, 90) * mm, "end": v(0, 120) * mm, "construction": true});
            skLineSegment(sketch, "E81", {"start": v(-33, 90) * mm, "end": v(-15, 108) * mm});
            skLineSegment(sketch, "E82", {"start": v(33, 90) * mm, "end": v(15, 108) * mm});
            skLineSegment(sketch, "E83", {"start": v(-15, 108) * mm, "end": v(-15, 120) * mm});
            skLineSegment(sketch, "E84", {"start": v(15, 108) * mm, "end": v(15, 120) * mm});
            skArc(sketch, "E85", {"start": v(-15, 120) * mm, "mid": v(0, 135) * mm, "end": v(15, 120) * mm});
            skCircle(sketch, "E86", {"center": v(0, 120) * mm, "radius": 6 * mm});
            skLineSegment(sketch, "E87", {"start": v(-141.48, 0) * mm, "end": v(150.94, 0) * mm, "construction": true});
            skPoint(sketch, "E87.endSnap0", {"position": v(80, 0) * mm});
            skLineSegment(sketch, "E88.MirrorCS", {"start": v(-33, -90) * mm, "end": v(-15, -108) * mm});
            skLineSegment(sketch, "E89.MirrorCS", {"start": v(-15, -108) * mm, "end": v(-15, -120) * mm});
            skArc(sketch, "E90.MirrorCS", {"start": v(-15, -120) * mm, "mid": v(0, -135) * mm, "end": v(15, -120) * mm});
            skLineSegment(sketch, "E91.MirrorCS", {"start": v(15, -108) * mm, "end": v(15, -120) * mm});
            skLineSegment(sketch, "E92.MirrorCS", {"start": v(33, -90) * mm, "end": v(15, -108) * mm});
            skCircle(sketch, "E93.MirrorC", {"center": v(0, -120) * mm, "radius": 6 * mm});
            skSolve(sketch);
        }
        {
            var Q0;
            {var subQ0=sQuery(id+"F16.wireOp",EDGE,"E81");Q0=makeQuery(id+"F16.imprint","IMPRINT",FACE,{"disambiguationData":[TD([[makeQuery(id+"F16.imprint","IMPRINT",EDGE,{"derivedFrom":subQ0}),-1.0]])]});}
            var Q1;
            Q1=makeQuery(id+"F16.imprint","IMPRINT",FACE,{"disambiguationData":[TD([[makeQuery(id+"F16.imprint","IMPRINT",EDGE,{"derivedFrom":sQuery(id+"F16.wireOp",EDGE,"E79.1")}),-1.0]])]});
            var Q2;
            {var subQ0=sQuery(id+"F16.wireOp",EDGE,"E88.MirrorCS");Q2=makeQuery(id+"F16.imprint","IMPRINT",FACE,{"disambiguationData":[TD([[makeQuery(id+"F16.imprint","IMPRINT",EDGE,{"derivedFrom":subQ0}),1.0]])]});}
            var Q3;
            Q3=makeQuery(id+"F2.opExtrude","CAP_FACE",FACE,{"disambiguationData":[OSD([sQuery(id+"F0.wireOp",EDGE,"E12"),sQuery(id+"F0.wireOp",EDGE,"E13"),sQuery(id+"F0.wireOp",EDGE,"E14"),sQuery(id+"F0.wireOp",EDGE,"E15"),sQuery(id+"F0.wireOp",EDGE,"E17.filletArc"),sQuery(id+"F0.wireOp",EDGE,"E18.filletArc"),sQuery(id+"F0.wireOp",EDGE,"E19.filletArc"),sQuery(id+"F0.wireOp",EDGE,"E20.filletArc"),sQuery(id+"F0.wireOp",EDGE,"E25.0"),sQuery(id+"F0.wireOp",EDGE,"E25.1"),sQuery(id+"F0.wireOp",EDGE,"E25.2"),sQuery(id+"F0.wireOp",EDGE,"E25.3"),sQuery(id+"F0.wireOp",EDGE,"E25.4"),sQuery(id+"F0.wireOp",EDGE,"E25.5"),sQuery(id+"F0.wireOp",EDGE,"E25.6"),sQuery(id+"F0.wireOp",EDGE,"E25.7")])],"isStart":false});
            extrude(context, id + "F17", {"entities" : qUnion([Q0, Q1, Q2]), "endBound" : BoundingType.UP_TO_SURFACE, "endBoundEntityFace" : qUnion([Q3]), "depth" : 25 * mm});
        }
    });
